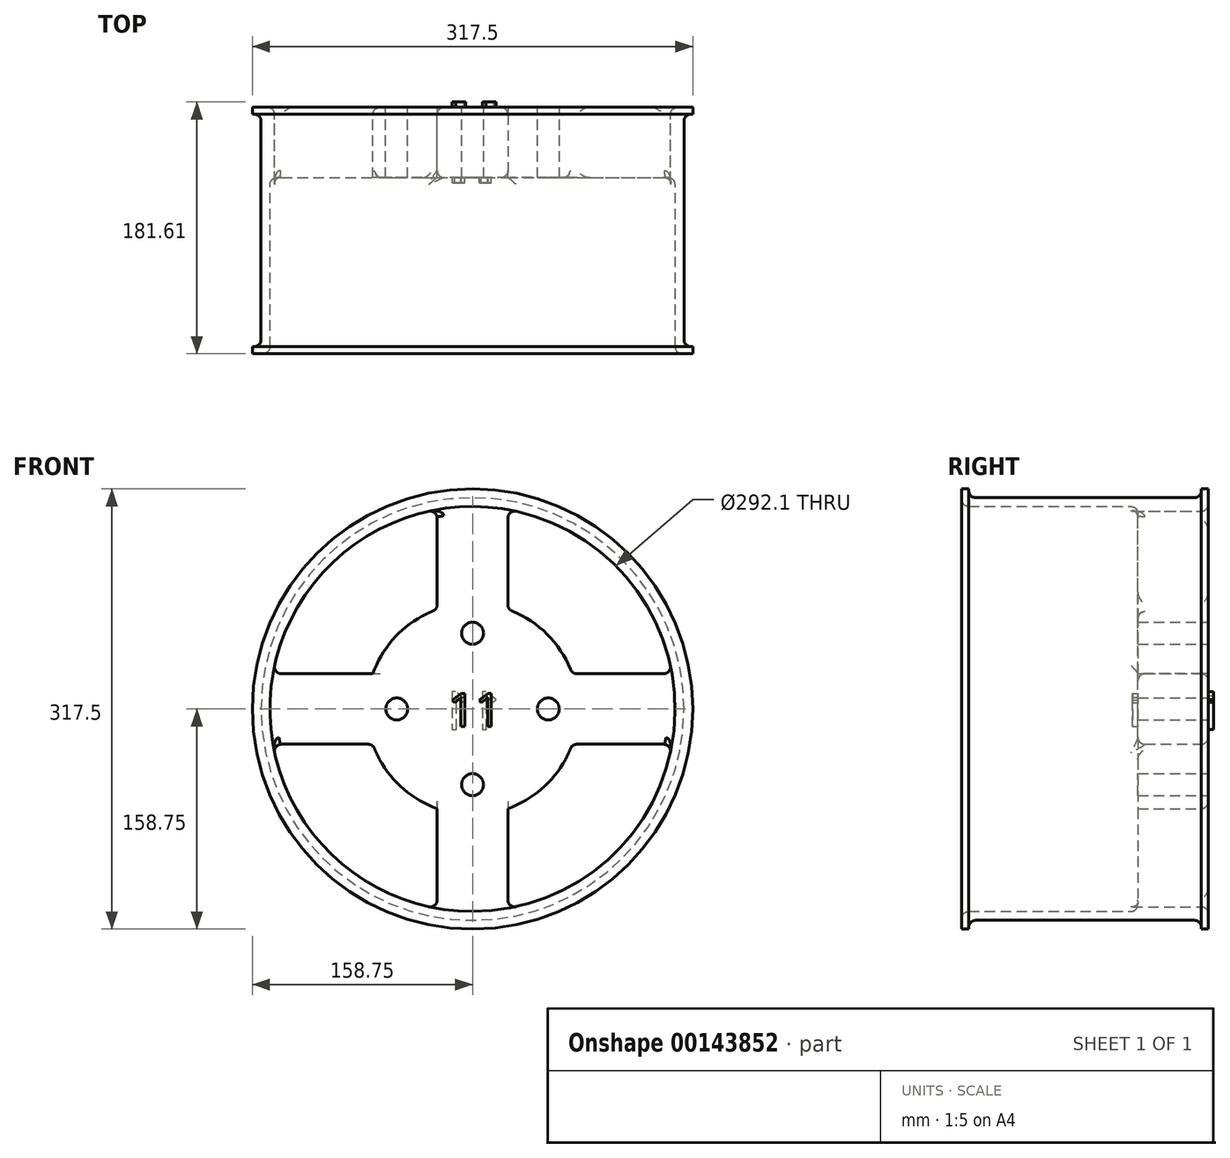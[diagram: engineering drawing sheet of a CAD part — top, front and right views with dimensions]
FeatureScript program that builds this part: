
annotation { "Feature Type Name" : "Feature", "Feature Type Description" : "" }
export const myFeature = defineFeature(function(context is Context, id is Id, definition is map)
    precondition{}
    {
        {
            var Q0;
            Q0=qCreatedBy(makeId("Front.planeOp"),FACE);
            var sketch = newSketch(context, id + "F0", { "sketchPlane" : qUnion([Q0])});
            skCircle(sketch, "E0", {"center": v(0, 0) * mm, "radius": 152.4 * mm});
            skCircle(sketch, "E1", {"center": v(0, 0) * mm, "radius": 76.2 * mm});
            skCircle(sketch, "E2", {"center": v(0, 0) * mm, "radius": 146.05 * mm});
            skCircle(sketch, "E3", {"center": v(0, 54.61) * mm, "radius": 7.94 * mm});
            skCircle(sketch, "E4", {"center": v(0, -54.61) * mm, "radius": 7.94 * mm});
            skLineSegment(sketch, "E5.0", {"start": v(-143.82, 25.4) * mm, "end": v(-71.84, 25.4) * mm});
            skLineSegment(sketch, "E6.0", {"start": v(-143.82, -25.4) * mm, "end": v(-71.84, -25.4) * mm});
            skLineSegment(sketch, "E7.0", {"start": v(-25.4, 71.84) * mm, "end": v(-25.4, 143.82) * mm});
            skLineSegment(sketch, "E7.1", {"start": v(-25.4, -71.84) * mm, "end": v(-25.4, -143.82) * mm});
            skLineSegment(sketch, "E8.0", {"start": v(25.4, 71.84) * mm, "end": v(25.4, 143.82) * mm});
            skLineSegment(sketch, "E8.1", {"start": v(25.4, -71.84) * mm, "end": v(25.4, -143.82) * mm});
            skCircle(sketch, "E9", {"center": v(-54.61, 0) * mm, "radius": 7.94 * mm});
            skCircle(sketch, "E10", {"center": v(54.61, 0) * mm, "radius": 7.94 * mm});
            skLineSegment(sketch, "E11.trimOffspring", {"start": v(71.84, 25.4) * mm, "end": v(143.82, 25.4) * mm});
            skLineSegment(sketch, "E12.trimOffspring", {"start": v(71.84, -25.4) * mm, "end": v(143.82, -25.4) * mm});
            skSolve(sketch);
        }
        {
            var Q0;
            Q0=makeQuery(id+"F0.imprint","IMPRINT",FACE,{"disambiguationData":[TD([[makeQuery(id+"F0.imprint","IMPRINT",EDGE,{"derivedFrom":sQuery(id+"F0.wireOp",EDGE,"E3")}),-1.0]])]});
            var Q1;
            {var subQ0=sQuery(id+"F0.wireOp",EDGE,"E7.0");Q1=makeQuery(id+"F0.imprint","IMPRINT",FACE,{"disambiguationData":[TD([[makeQuery(id+"F0.imprint","IMPRINT",EDGE,{"derivedFrom":subQ0}),-1.0]])]});}
            var Q2;
            {var subQ0=sQuery(id+"F0.wireOp",EDGE,"E5.0");Q2=makeQuery(id+"F0.imprint","IMPRINT",FACE,{"disambiguationData":[TD([[makeQuery(id+"F0.imprint","IMPRINT",EDGE,{"derivedFrom":subQ0}),-1.0]])]});}
            var Q3;
            {var subQ0=sQuery(id+"F0.wireOp",EDGE,"E7.1");Q3=makeQuery(id+"F0.imprint","IMPRINT",FACE,{"disambiguationData":[TD([[makeQuery(id+"F0.imprint","IMPRINT",EDGE,{"derivedFrom":subQ0}),1.0]])]});}
            var Q4;
            {var subQ0=sQuery(id+"F0.wireOp",EDGE,"E11.trimOffspring");Q4=makeQuery(id+"F0.imprint","IMPRINT",FACE,{"disambiguationData":[TD([[makeQuery(id+"F0.imprint","IMPRINT",EDGE,{"derivedFrom":subQ0}),-1.0]])]});}
            extrude(context, id + "F1", {"entities" : qUnion([Q0, Q1, Q2, Q3, Q4]), "depth" : 50.8 * mm});
        }
        {
            var Q0;
            Q0=makeQuery(id+"F0.imprint","IMPRINT",FACE,{"disambiguationData":[TD([[makeQuery(id+"F0.imprint","IMPRINT",EDGE,{"derivedFrom":sQuery(id+"F0.wireOp",EDGE,"E0")}),1.0]])]});
            extrude(context, id + "F2", {"entities" : qUnion([Q0]), "operationType" : NewBodyOperationType.ADD, "depth" : 177.8 * mm});
        }
        {
            var Q0;
            Q0=makeQuery(id+"F2.opExtrude","SWEPT_FACE",FACE,{"disambiguationData":[OSD([sQuery(id+"F0.wireOp",EDGE,"E2")])]});
            fillet(context, id + "F3", {"entities" : qUnion([Q0]), "radius" : 5.08 * mm, "tangentPropagation" : true, "allowEdgeOverflow" : false});
        }
        {
            var Q0;
            {var subQ0=sQuery(id+"F0.wireOp",EDGE,"E1");Q0=makeQuery(id+"F1.opExtrude","SWEPT_FACE",FACE,{"disambiguationData":[OSD([subQ0]),TDD([makeQuery(id+"F0.imprint","IMPRINT",EDGE,{"disambiguationData":[TD([[makeQuery(id+"F0.imprint","INTERSECT",VERTEX,{"derivedFrom":[subQ0,sQuery(id+"F0.wireOp",EDGE,"E8.0")]}),1.0]])],"derivedFrom":subQ0})])]});}
            fillet(context, id + "F4", {"entities" : qUnion([Q0]), "radius" : 5.08 * mm, "tangentPropagation" : true, "allowEdgeOverflow" : false});
        }
        {
            var Q0;
            Q0=makeQuery(id+"F1.opExtrude","SWEPT_FACE",FACE,{"disambiguationData":[OSD([sQuery(id+"F0.wireOp",EDGE,"E7.0")])]});
            fillet(context, id + "F5", {"entities" : qUnion([Q0]), "radius" : 5.08 * mm, "tangentPropagation" : true, "allowEdgeOverflow" : false});
        }
        {
            var Q0;
            Q0=makeQuery(id+"F1.opExtrude","SWEPT_FACE",FACE,{"disambiguationData":[OSD([sQuery(id+"F0.wireOp",EDGE,"E12.trimOffspring")])]});
            fillet(context, id + "F6", {"entities" : qUnion([Q0]), "radius" : 5.08 * mm, "tangentPropagation" : true, "allowEdgeOverflow" : false});
        }
        {
            var Q0;
            Q0=makeQuery(id+"F1.opExtrude","SWEPT_FACE",FACE,{"disambiguationData":[OSD([sQuery(id+"F0.wireOp",EDGE,"E6.0")])]});
            fillet(context, id + "F7", {"entities" : qUnion([Q0]), "radius" : 5.08 * mm, "tangentPropagation" : true, "allowEdgeOverflow" : false});
        }
        {
            var Q0;
            {var subQ0=sQuery(id+"F0.wireOp",EDGE,"E1");Q0=makeQuery(id+"F1.opExtrude","CAP_EDGE",EDGE,{"disambiguationData":[OSD([subQ0]),TDD([makeQuery(id+"F0.imprint","IMPRINT",EDGE,{"disambiguationData":[TD([[makeQuery(id+"F0.imprint","INTERSECT",VERTEX,{"derivedFrom":[subQ0,sQuery(id+"F0.wireOp",EDGE,"E5.0")]}),1.0]])],"derivedFrom":subQ0})])],"isStart":true});}
            var Q1;
            {var subQ0=sQuery(id+"F0.wireOp",EDGE,"E1");Q1=makeQuery(id+"F1.opExtrude","CAP_EDGE",EDGE,{"disambiguationData":[OSD([subQ0]),TDD([makeQuery(id+"F0.imprint","IMPRINT",EDGE,{"disambiguationData":[TD([[makeQuery(id+"F0.imprint","INTERSECT",VERTEX,{"derivedFrom":[subQ0,sQuery(id+"F0.wireOp",EDGE,"E6.0")]}),-1.0]])],"derivedFrom":subQ0})])],"isStart":true});}
            var Q2;
            {var subQ0=sQuery(id+"F0.wireOp",EDGE,"E1");Q2=makeQuery(id+"F1.opExtrude","CAP_EDGE",EDGE,{"disambiguationData":[OSD([subQ0]),TDD([makeQuery(id+"F0.imprint","IMPRINT",EDGE,{"disambiguationData":[TD([[makeQuery(id+"F0.imprint","INTERSECT",VERTEX,{"derivedFrom":[subQ0,sQuery(id+"F0.wireOp",EDGE,"E8.1")]}),-1.0]])],"derivedFrom":subQ0})])],"isStart":true});}
            fillet(context, id + "F8", {"entities" : qUnion([Q0, Q1, Q2]), "radius" : 5.08 * mm, "tangentPropagation" : true, "allowEdgeOverflow" : false});
        }
        {
            var Q0;
            Q0=makeQuery(id+"F0.imprint","IMPRINT",FACE,{"disambiguationData":[TD([[makeQuery(id+"F0.imprint","IMPRINT",EDGE,{"derivedFrom":sQuery(id+"F0.wireOp",EDGE,"E0")}),1.0]])]});
            var sketch = newSketch(context, id + "F9", { "sketchPlane" : qUnion([Q0])});
            skCircle(sketch, "E13", {"center": v(0, 0) * mm, "radius": 158.75 * mm});
            skSolve(sketch);
        }
        {
            var Q0;
            Q0=makeQuery(id+"F9.imprint","IMPRINT",FACE,{"disambiguationData":[TD([[makeQuery(id+"F9.imprint","IMPRINT",EDGE,{"derivedFrom":sQuery(id+"F9.wireOp",EDGE,"E13")}),1.0]])]});
            extrude(context, id + "F10", {"entities" : qUnion([Q0]), "operationType" : NewBodyOperationType.ADD, "depth" : 5.08 * mm});
        }
        {
            var Q0;
            Q0=makeQuery(id+"F2.opExtrude","CAP_FACE",FACE,{"disambiguationData":[OSD([sQuery(id+"F0.wireOp",EDGE,"E0"),sQuery(id+"F0.wireOp",EDGE,"E2")])],"isStart":false});
            var sketch = newSketch(context, id + "F11", { "sketchPlane" : qUnion([Q0])});
            skCircle(sketch, "E14", {"center": v(0, 0) * mm, "radius": 158.75 * mm});
            skSolve(sketch);
        }
        {
            var Q0;
            Q0=makeQuery(id+"F11.imprint","IMPRINT",FACE,{"disambiguationData":[TD([[makeQuery(id+"F11.imprint","IMPRINT",EDGE,{"derivedFrom":sQuery(id+"F11.wireOp",EDGE,"E14")}),1.0]])]});
            extrude(context, id + "F12", {"entities" : qUnion([Q0]), "operationType" : NewBodyOperationType.ADD, "oppositeDirection" : true, "depth" : 5.08 * mm});
        }
        {
            var Q0;
            Q0=makeQuery(id+"F1.opExtrude","CAP_FACE",FACE,{"disambiguationData":[OSD([sQuery(id+"F0.wireOp",EDGE,"E1"),sQuery(id+"F0.wireOp",EDGE,"E2"),sQuery(id+"F0.wireOp",EDGE,"E3"),sQuery(id+"F0.wireOp",EDGE,"E4"),sQuery(id+"F0.wireOp",EDGE,"E5.0"),sQuery(id+"F0.wireOp",EDGE,"E6.0"),sQuery(id+"F0.wireOp",EDGE,"E7.0"),sQuery(id+"F0.wireOp",EDGE,"E7.1"),sQuery(id+"F0.wireOp",EDGE,"E8.0"),sQuery(id+"F0.wireOp",EDGE,"E8.1"),sQuery(id+"F0.wireOp",EDGE,"E9"),sQuery(id+"F0.wireOp",EDGE,"E10"),sQuery(id+"F0.wireOp",EDGE,"E11.trimOffspring"),sQuery(id+"F0.wireOp",EDGE,"E12.trimOffspring")])],"isStart":false});
            var sketch = newSketch(context, id + "F13", { "sketchPlane" : qUnion([Q0])});
            skText(sketch, "E15", { "text": "11", "fontName": "OpenSans-Regular.ttf"});
            const initialGuessF13  = {"E15": [-0.01739, -0.0127, 1, 0, 0.02416]};
            skSetInitialGuess(sketch, initialGuessF13);
            skSolve(sketch);
        }
        {
            var Q0;
            Q0 = qSketchRegion(id + "F13", true);
            extrude(context, id + "F14", {"entities" : qUnion([Q0]), "operationType" : NewBodyOperationType.ADD, "depth" : 3.8 * mm});
        }
        {
            var Q0;
            {var subQ0=sQuery(id+"F0.wireOp",EDGE,"E0");var subQ1=sQuery(id+"F0.wireOp",EDGE,"E2");Q0=makeQuery(id+"F10.boolean.opBoolean","MERGE",FACE,{"derivedFrom":[makeQuery(id+"F2.boolean.opBoolean","MERGE",FACE,{"derivedFrom":[makeQuery(id+"F1.opExtrude","CAP_FACE",FACE,{"disambiguationData":[OSD([sQuery(id+"F0.wireOp",EDGE,"E1"),subQ1,sQuery(id+"F0.wireOp",EDGE,"E3"),sQuery(id+"F0.wireOp",EDGE,"E4"),sQuery(id+"F0.wireOp",EDGE,"E5.0"),sQuery(id+"F0.wireOp",EDGE,"E6.0"),sQuery(id+"F0.wireOp",EDGE,"E7.0"),sQuery(id+"F0.wireOp",EDGE,"E7.1"),sQuery(id+"F0.wireOp",EDGE,"E8.0"),sQuery(id+"F0.wireOp",EDGE,"E8.1"),sQuery(id+"F0.wireOp",EDGE,"E9"),sQuery(id+"F0.wireOp",EDGE,"E10"),sQuery(id+"F0.wireOp",EDGE,"E11.trimOffspring"),sQuery(id+"F0.wireOp",EDGE,"E12.trimOffspring")])],"isStart":true}),makeQuery(id+"F2.opExtrude","CAP_FACE",FACE,{"disambiguationData":[OSD([subQ0,subQ1])],"isStart":true})]}),makeQuery(id+"F10.opExtrude","CAP_FACE",FACE,{"disambiguationData":[OSD([subQ0,sQuery(id+"F9.wireOp",EDGE,"E13")])],"isStart":true})]});}
            var sketch = newSketch(context, id + "F15", { "sketchPlane" : qUnion([Q0])});
            skText(sketch, "E16", { "text": "11", "fontName": "OpenSans-Regular.ttf"});
            const initialGuessF15  = {"E16": [-0.02036, -0.01473, 1, 0, 0.02742]};
            skSetInitialGuess(sketch, initialGuessF15);
            skSolve(sketch);
        }
        {
            var Q0;
            Q0 = qSketchRegion(id + "F15", true);
            extrude(context, id + "F16", {"entities" : qUnion([Q0]), "operationType" : NewBodyOperationType.ADD, "depth" : 3.8 * mm});
        }
        {
            var Q0;
            Q0=makeQuery(id+"F2.opExtrude","SWEPT_FACE",FACE,{"disambiguationData":[OSD([sQuery(id+"F0.wireOp",EDGE,"E0")])]});
            fillet(context, id + "F17", {"entities" : qUnion([Q0]), "radius" : 5.08 * mm, "tangentPropagation" : true, "allowEdgeOverflow" : false});
        }
    });
